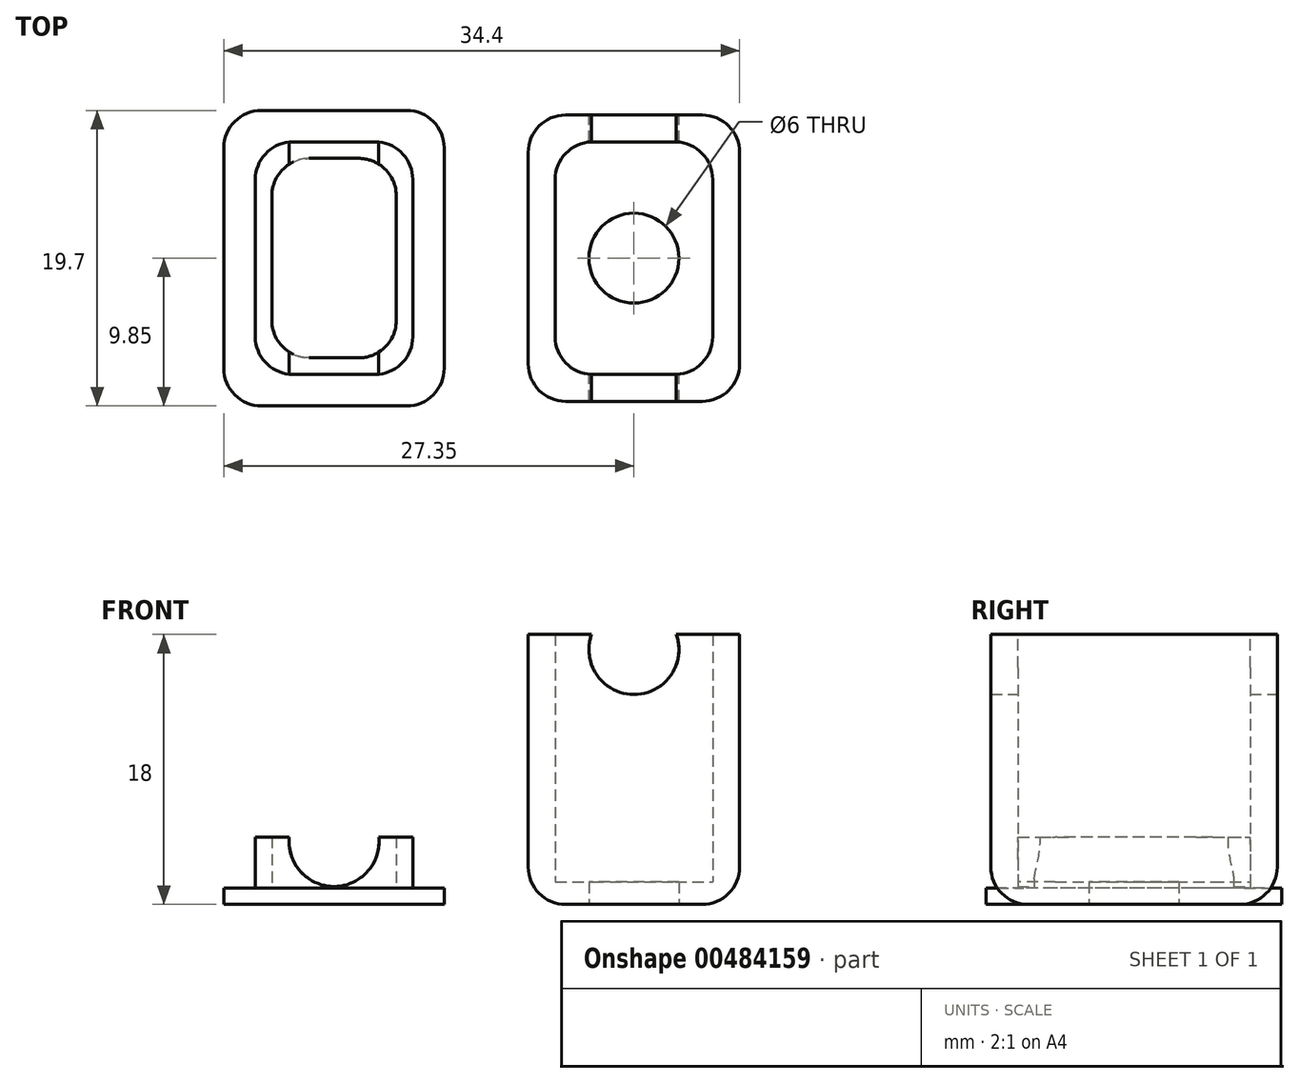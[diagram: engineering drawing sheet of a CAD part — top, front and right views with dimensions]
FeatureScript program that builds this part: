
annotation { "Feature Type Name" : "Feature", "Feature Type Description" : "" }
export const myFeature = defineFeature(function(context is Context, id is Id, definition is map)
    precondition{}
    {
        {
            var Q0;
            Q0=qCreatedBy(makeId("Top.planeOp"),FACE);
            var sketch = newSketch(context, id + "F0", { "sketchPlane" : qUnion([Q0])});
            skLineSegment(sketch, "E0.bottom", {"start": v(-5.25, -7.75) * mm, "end": v(5.25, -7.75) * mm});
            skLineSegment(sketch, "E0.top", {"start": v(-5.25, 7.75) * mm, "end": v(5.25, 7.75) * mm});
            skLineSegment(sketch, "E0.left", {"start": v(-5.25, -7.75) * mm, "end": v(-5.25, 7.75) * mm});
            skLineSegment(sketch, "E0.right", {"start": v(5.25, -7.75) * mm, "end": v(5.25, 7.75) * mm});
            skPoint(sketch, "E0.middle", {"position": v(0, 0) * mm});
            skLineSegment(sketch, "E1.0", {"start": v(7.05, -9.55) * mm, "end": v(7.05, 9.55) * mm});
            skLineSegment(sketch, "E1.1", {"start": v(-7.05, -9.55) * mm, "end": v(7.05, -9.55) * mm});
            skLineSegment(sketch, "E1.2", {"start": v(-7.05, -9.55) * mm, "end": v(-7.05, 9.55) * mm});
            skLineSegment(sketch, "E1.3", {"start": v(-7.05, 9.55) * mm, "end": v(7.05, 9.55) * mm});
            skCircle(sketch, "E2", {"center": v(0, 0) * mm, "radius": 3 * mm});
            skLineSegment(sketch, "E3.bottom", {"start": v(-25.25, 7.75) * mm, "end": v(-14.75, 7.75) * mm});
            skLineSegment(sketch, "E3.top", {"start": v(-25.25, -7.75) * mm, "end": v(-14.75, -7.75) * mm});
            skLineSegment(sketch, "E3.left", {"start": v(-25.25, 7.75) * mm, "end": v(-25.25, -7.75) * mm});
            skLineSegment(sketch, "E3.right", {"start": v(-14.75, 7.75) * mm, "end": v(-14.75, -7.75) * mm});
            skPoint(sketch, "E3.middle", {"position": v(-20, 0) * mm});
            skLineSegment(sketch, "E4.0", {"start": v(-27.35, 9.85) * mm, "end": v(-12.65, 9.85) * mm});
            skLineSegment(sketch, "E4.1", {"start": v(-27.35, 9.85) * mm, "end": v(-27.35, -9.85) * mm});
            skLineSegment(sketch, "E4.2", {"start": v(-27.35, -9.85) * mm, "end": v(-12.65, -9.85) * mm});
            skLineSegment(sketch, "E4.3", {"start": v(-12.65, 9.85) * mm, "end": v(-12.65, -9.85) * mm});
            skLineSegment(sketch, "E5.0", {"start": v(-24.15, 6.65) * mm, "end": v(-15.85, 6.65) * mm});
            skLineSegment(sketch, "E5.1", {"start": v(-24.15, 6.65) * mm, "end": v(-24.15, -6.65) * mm});
            skLineSegment(sketch, "E5.2", {"start": v(-24.15, -6.65) * mm, "end": v(-15.85, -6.65) * mm});
            skLineSegment(sketch, "E5.3", {"start": v(-15.85, 6.65) * mm, "end": v(-15.85, -6.65) * mm});
            skLineSegment(sketch, "E6", {"start": v(0, 0) * mm, "end": v(-20, 0) * mm, "construction": true});
            skSolve(sketch);
        }
        {
            var Q0;
            Q0=makeQuery(id+"F0.imprint","IMPRINT",FACE,{"disambiguationData":[TD([[makeQuery(id+"F0.imprint","IMPRINT",EDGE,{"derivedFrom":sQuery(id+"F0.wireOp",EDGE,"E0.bottom")}),1.0]])]});
            extrude(context, id + "F1", {"entities" : qUnion([Q0]), "depth" : 1.5 * mm});
        }
        {
            var Q0;
            Q0=makeQuery(id+"F0.imprint","IMPRINT",FACE,{"disambiguationData":[TD([[makeQuery(id+"F0.imprint","IMPRINT",EDGE,{"derivedFrom":sQuery(id+"F0.wireOp",EDGE,"E0.bottom")}),-1.0]])]});
            extrude(context, id + "F2", {"entities" : qUnion([Q0]), "operationType" : NewBodyOperationType.ADD, "depth" : 18 * mm});
        }
        {
            var Q0;
            Q0=makeQuery(id+"F0.imprint","IMPRINT",FACE,{"disambiguationData":[TD([[makeQuery(id+"F0.imprint","IMPRINT",EDGE,{"derivedFrom":sQuery(id+"F0.wireOp",EDGE,"E3.bottom")}),1.0]])]});
            var Q1;
            Q1=makeQuery(id+"F0.imprint","IMPRINT",FACE,{"disambiguationData":[TD([[makeQuery(id+"F0.imprint","IMPRINT",EDGE,{"derivedFrom":sQuery(id+"F0.wireOp",EDGE,"E5.0")}),-1.0]])]});
            extrude(context, id + "F3", {"entities" : qUnion([Q0, Q1]), "depth" : 1.1 * mm});
        }
        {
            var Q0;
            Q0=makeQuery(id+"F0.imprint","IMPRINT",FACE,{"disambiguationData":[TD([[makeQuery(id+"F0.imprint","IMPRINT",EDGE,{"derivedFrom":sQuery(id+"F0.wireOp",EDGE,"E3.bottom")}),-1.0]])]});
            extrude(context, id + "F4", {"entities" : qUnion([Q0]), "operationType" : NewBodyOperationType.ADD, "depth" : 4.5 * mm});
        }
        {
            var Q0;
            Q0=makeQuery(id+"F2.opExtrude","CAP_EDGE",EDGE,{"disambiguationData":[OSD([sQuery(id+"F0.wireOp",EDGE,"E1.0")])],"isStart":true});
            var Q1;
            Q1=makeQuery(id+"F2.opExtrude","SWEPT_EDGE",EDGE,{"disambiguationData":[OSD([sQuery(id+"F0.wireOp",EDGE,"E1.0"),sQuery(id+"F0.wireOp",EDGE,"E1.3")])]});
            var Q2;
            Q2=makeQuery(id+"F2.opExtrude","CAP_EDGE",EDGE,{"disambiguationData":[OSD([sQuery(id+"F0.wireOp",EDGE,"E1.3")])],"isStart":true});
            var Q3;
            Q3=makeQuery(id+"F2.opExtrude","CAP_EDGE",EDGE,{"disambiguationData":[OSD([sQuery(id+"F0.wireOp",EDGE,"E1.2")])],"isStart":true});
            var Q4;
            Q4=makeQuery(id+"F2.opExtrude","SWEPT_EDGE",EDGE,{"disambiguationData":[OSD([sQuery(id+"F0.wireOp",EDGE,"E1.0"),sQuery(id+"F0.wireOp",EDGE,"E1.1")])]});
            var Q5;
            Q5=makeQuery(id+"F2.opExtrude","SWEPT_EDGE",EDGE,{"disambiguationData":[OSD([sQuery(id+"F0.wireOp",EDGE,"E1.1"),sQuery(id+"F0.wireOp",EDGE,"E1.2")])]});
            var Q6;
            Q6=makeQuery(id+"F2.opExtrude","CAP_EDGE",EDGE,{"disambiguationData":[OSD([sQuery(id+"F0.wireOp",EDGE,"E1.1")])],"isStart":true});
            var Q7;
            Q7=makeQuery(id+"F2.opExtrude","SWEPT_EDGE",EDGE,{"disambiguationData":[OSD([sQuery(id+"F0.wireOp",EDGE,"E1.2"),sQuery(id+"F0.wireOp",EDGE,"E1.3")])]});
            var Q8;
            Q8=makeQuery(id+"F2.opExtrude","SWEPT_EDGE",EDGE,{"disambiguationData":[OSD([sQuery(id+"F0.wireOp",EDGE,"E0.top"),sQuery(id+"F0.wireOp",EDGE,"E0.left")])]});
            var Q9;
            Q9=makeQuery(id+"F2.opExtrude","SWEPT_EDGE",EDGE,{"disambiguationData":[OSD([sQuery(id+"F0.wireOp",EDGE,"E0.top"),sQuery(id+"F0.wireOp",EDGE,"E0.right")])]});
            var Q10;
            Q10=makeQuery(id+"F2.opExtrude","SWEPT_EDGE",EDGE,{"disambiguationData":[OSD([sQuery(id+"F0.wireOp",EDGE,"E0.bottom"),sQuery(id+"F0.wireOp",EDGE,"E0.right")])]});
            var Q11;
            Q11=makeQuery(id+"F2.opExtrude","SWEPT_EDGE",EDGE,{"disambiguationData":[OSD([sQuery(id+"F0.wireOp",EDGE,"E0.bottom"),sQuery(id+"F0.wireOp",EDGE,"E0.left")])]});
            var Q12;
            Q12=makeQuery(id+"F3.opExtrude","SWEPT_EDGE",EDGE,{"disambiguationData":[OSD([sQuery(id+"F0.wireOp",EDGE,"E4.2"),sQuery(id+"F0.wireOp",EDGE,"E4.3")])]});
            var Q13;
            Q13=makeQuery(id+"F3.opExtrude","SWEPT_EDGE",EDGE,{"disambiguationData":[OSD([sQuery(id+"F0.wireOp",EDGE,"E4.1"),sQuery(id+"F0.wireOp",EDGE,"E4.2")])]});
            var Q14;
            Q14=makeQuery(id+"F4.opExtrude","SWEPT_EDGE",EDGE,{"disambiguationData":[OSD([sQuery(id+"F0.wireOp",EDGE,"E3.top"),sQuery(id+"F0.wireOp",EDGE,"E3.right")])]});
            var Q15;
            Q15=makeQuery(id+"F4.opExtrude","SWEPT_EDGE",EDGE,{"disambiguationData":[OSD([sQuery(id+"F0.wireOp",EDGE,"E5.2"),sQuery(id+"F0.wireOp",EDGE,"E5.3")])]});
            var Q16;
            Q16=makeQuery(id+"F4.opExtrude","SWEPT_EDGE",EDGE,{"disambiguationData":[OSD([sQuery(id+"F0.wireOp",EDGE,"E5.0"),sQuery(id+"F0.wireOp",EDGE,"E5.3")])]});
            var Q17;
            Q17=makeQuery(id+"F4.opExtrude","SWEPT_EDGE",EDGE,{"disambiguationData":[OSD([sQuery(id+"F0.wireOp",EDGE,"E5.0"),sQuery(id+"F0.wireOp",EDGE,"E5.1")])]});
            var Q18;
            Q18=makeQuery(id+"F3.opExtrude","SWEPT_EDGE",EDGE,{"disambiguationData":[OSD([sQuery(id+"F0.wireOp",EDGE,"E4.0"),sQuery(id+"F0.wireOp",EDGE,"E4.3")])]});
            var Q19;
            Q19=makeQuery(id+"F4.opExtrude","SWEPT_EDGE",EDGE,{"disambiguationData":[OSD([sQuery(id+"F0.wireOp",EDGE,"E3.bottom"),sQuery(id+"F0.wireOp",EDGE,"E3.right")])]});
            var Q20;
            Q20=makeQuery(id+"F4.opExtrude","SWEPT_EDGE",EDGE,{"disambiguationData":[OSD([sQuery(id+"F0.wireOp",EDGE,"E5.1"),sQuery(id+"F0.wireOp",EDGE,"E5.2")])]});
            var Q21;
            Q21=makeQuery(id+"F4.opExtrude","SWEPT_EDGE",EDGE,{"disambiguationData":[OSD([sQuery(id+"F0.wireOp",EDGE,"E3.bottom"),sQuery(id+"F0.wireOp",EDGE,"E3.left")])]});
            var Q22;
            Q22=makeQuery(id+"F3.opExtrude","SWEPT_EDGE",EDGE,{"disambiguationData":[OSD([sQuery(id+"F0.wireOp",EDGE,"E4.0"),sQuery(id+"F0.wireOp",EDGE,"E4.1")])]});
            var Q23;
            Q23=makeQuery(id+"F4.opExtrude","SWEPT_EDGE",EDGE,{"disambiguationData":[OSD([sQuery(id+"F0.wireOp",EDGE,"E3.top"),sQuery(id+"F0.wireOp",EDGE,"E3.left")])]});
            fillet(context, id + "F5", {"entities" : qUnion([Q0, Q1, Q2, Q3, Q4, Q5, Q6, Q7, Q8, Q9, Q10, Q11, Q12, Q13, Q14, Q15, Q16, Q17, Q18, Q19, Q20, Q21, Q22, Q23]), "radius" : 2.5 * mm, "tangentPropagation" : true, "allowEdgeOverflow" : false});
        }
        {
            var Q0;
            Q0=qCreatedBy(makeId("Front.planeOp"),FACE);
            var sketch = newSketch(context, id + "F6", { "sketchPlane" : qUnion([Q0])});
            skLineSegment(sketch, "E7", {"start": v(0, 0) * mm, "end": v(0, 17) * mm, "construction": true});
            skCircle(sketch, "E8", {"center": v(0, 17) * mm, "radius": 3 * mm});
            skLineSegment(sketch, "E9", {"start": v(0, 0) * mm, "end": v(-20, 0) * mm, "construction": true});
            skLineSegment(sketch, "E10", {"start": v(-20, 0) * mm, "end": v(-20, 4.2) * mm, "construction": true});
            skCircle(sketch, "E11", {"center": v(-20, 4.2) * mm, "radius": 3 * mm});
            skSolve(sketch);
        }
        {
            var Q0;
            Q0 = qSketchRegion(id + "F6", true);
            extrude(context, id + "F7", {"entities" : qUnion([Q0]), "operationType" : NewBodyOperationType.REMOVE, "endBound" : BoundingType.SYMMETRIC, "depth" : 25 * mm});
        }
    });
